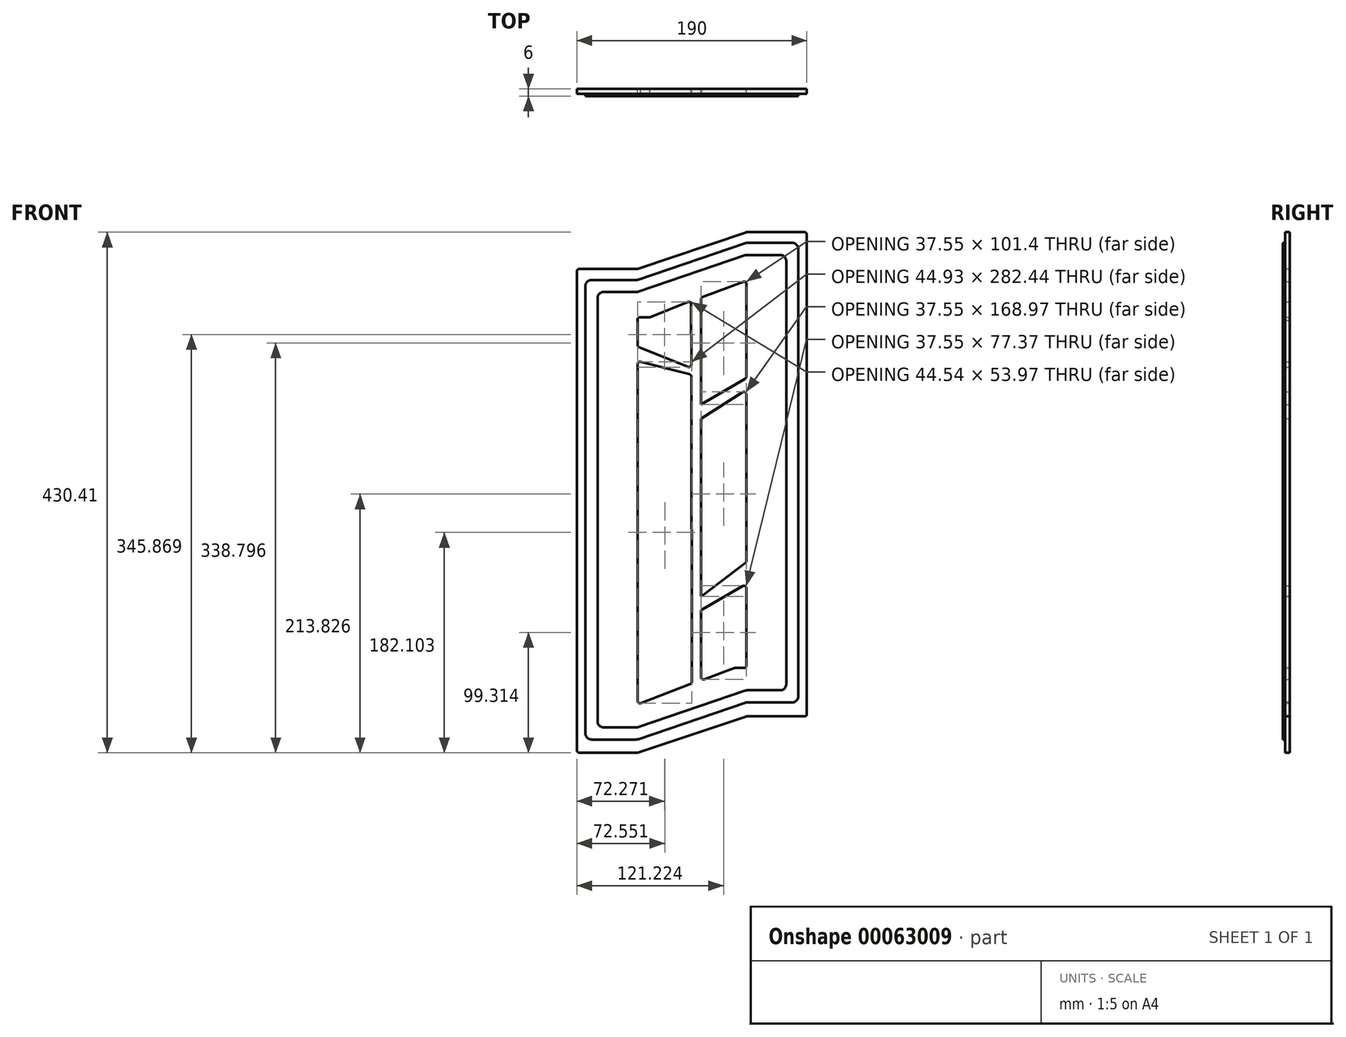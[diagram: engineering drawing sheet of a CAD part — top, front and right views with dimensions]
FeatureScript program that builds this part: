
annotation { "Feature Type Name" : "Feature", "Feature Type Description" : "" }
export const myFeature = defineFeature(function(context is Context, id is Id, definition is map)
    precondition{}
    {
        {
            var Q0;
            Q0=qCreatedBy(makeId("Front.planeOp"),FACE);
            var sketch = newSketch(context, id + "F0", { "sketchPlane" : qUnion([Q0])});
            skLineSegment(sketch, "E0", {"start": v(-0.33, 77.55) * mm, "end": v(-48, 77.55) * mm});
            skLineSegment(sketch, "E1", {"start": v(0.31, 77.65) * mm, "end": v(89.69, 107.86) * mm});
            skLineSegment(sketch, "E2", {"start": v(90.33, 107.96) * mm, "end": v(138, 107.96) * mm});
            skLineSegment(sketch, "E3", {"start": v(-48, -322.45) * mm, "end": v(-0.32, -322.45) * mm});
            skLineSegment(sketch, "E4", {"start": v(0.3, -322.35) * mm, "end": v(89.7, -292.56) * mm});
            skLineSegment(sketch, "E5", {"start": v(90.32, -292.45) * mm, "end": v(138, -292.45) * mm});
            skLineSegment(sketch, "E6", {"start": v(140, -290.45) * mm, "end": v(140, 105.96) * mm});
            skLineSegment(sketch, "E7", {"start": v(90, 107.96) * mm, "end": v(90, 67.96) * mm, "construction": true});
            skLineSegment(sketch, "E8", {"start": v(0, -322.45) * mm, "end": v(0, -282.45) * mm, "construction": true});
            skLineSegment(sketch, "E9", {"start": v(90, -292.45) * mm, "end": v(90, -252.45) * mm, "construction": true});
            skLineSegment(sketch, "E10", {"start": v(0, 77.55) * mm, "end": v(0, 37.55) * mm, "construction": true});
            skLineSegment(sketch, "E11", {"start": v(2, 37.55) * mm, "end": v(9.63, 37.55) * mm});
            skLineSegment(sketch, "E12", {"start": v(88, -252.45) * mm, "end": v(80.36, -252.45) * mm});
            skLineSegment(sketch, "E13", {"start": v(90, 65.06) * mm, "end": v(90, -250.45) * mm});
            skLineSegment(sketch, "E14", {"start": v(0, -322.45) * mm, "end": v(140, -322.45) * mm, "construction": true});
            skLineSegment(sketch, "E15", {"start": v(140, -322.45) * mm, "end": v(140, -292.45) * mm, "construction": true});
            skLineSegment(sketch, "E16", {"start": v(-50, -322.45) * mm, "end": v(-50, -361.13) * mm, "construction": true});
            skLineSegment(sketch, "E17", {"start": v(-50, -361.13) * mm, "end": v(140, -361.13) * mm, "construction": true});
            skLineSegment(sketch, "E18", {"start": v(140, -361.13) * mm, "end": v(140, -322.45) * mm, "construction": true});
            skLineSegment(sketch, "E19", {"start": v(90, 107.96) * mm, "end": v(-50, 107.96) * mm, "construction": true});
            skLineSegment(sketch, "E20", {"start": v(-50, 107.96) * mm, "end": v(-50, 77.55) * mm, "construction": true});
            skPoint(sketch, "E21.visualSharp", {"position": v(90, 67.96) * mm});
            skArc(sketch, "E21.filletArc", {"start": v(90, 65.06) * mm, "mid": v(89.14, 66.7) * mm, "end": v(87.29, 66.93) * mm});
            skPoint(sketch, "E22.visualSharp", {"position": v(10, 37.55) * mm});
            skArc(sketch, "E22.filletArc", {"start": v(9.63, 37.55) * mm, "mid": v(10, 37.58) * mm, "end": v(10.34, 37.68) * mm});
            skPoint(sketch, "E23.visualSharp", {"position": v(0, 37.55) * mm});
            skArc(sketch, "E23.filletArc", {"start": v(2, 37.55) * mm, "mid": v(0.4, 36.74) * mm, "end": v(0.09, 34.96) * mm});
            skPoint(sketch, "E24.visualSharp", {"position": v(0, -282.45) * mm});
            skArc(sketch, "E24.filletArc", {"start": v(0.09, -280.15) * mm, "mid": v(1.12, -281.36) * mm, "end": v(2.7, -281.44) * mm});
            skPoint(sketch, "E25.visualSharp", {"position": v(80, -252.45) * mm});
            skArc(sketch, "E25.filletArc", {"start": v(80.36, -252.45) * mm, "mid": v(80, -252.49) * mm, "end": v(79.66, -252.58) * mm});
            skPoint(sketch, "E26.visualSharp", {"position": v(90, -252.45) * mm});
            skArc(sketch, "E26.filletArc", {"start": v(88, -252.45) * mm, "mid": v(89.41, -251.87) * mm, "end": v(90, -250.45) * mm});
            skPoint(sketch, "E27.visualSharp", {"position": v(140, 107.96) * mm});
            skArc(sketch, "E27.filletArc", {"start": v(140, 105.96) * mm, "mid": v(139.41, 107.37) * mm, "end": v(138, 107.96) * mm});
            skPoint(sketch, "E28.visualSharp", {"position": v(90, 107.96) * mm});
            skArc(sketch, "E28.filletArc", {"start": v(90.33, 107.96) * mm, "mid": v(90, 107.93) * mm, "end": v(89.69, 107.86) * mm});
            skPoint(sketch, "E29.visualSharp", {"position": v(0, 77.55) * mm});
            skArc(sketch, "E29.filletArc", {"start": v(-0.33, 77.55) * mm, "mid": v(0, 77.57) * mm, "end": v(0.31, 77.65) * mm});
            skPoint(sketch, "E30.visualSharp", {"position": v(-50, 77.55) * mm});
            skArc(sketch, "E30.filletArc", {"start": v(-48, 77.55) * mm, "mid": v(-49.41, 76.96) * mm, "end": v(-50, 75.55) * mm});
            skPoint(sketch, "E31.visualSharp", {"position": v(-50, -322.45) * mm});
            skArc(sketch, "E31.filletArc", {"start": v(-50, -320.45) * mm, "mid": v(-49.41, -321.87) * mm, "end": v(-48, -322.45) * mm});
            skPoint(sketch, "E32.visualSharp", {"position": v(0, -322.45) * mm});
            skArc(sketch, "E32.filletArc", {"start": v(-0.32, -322.45) * mm, "mid": v(0, -322.43) * mm, "end": v(0.3, -322.35) * mm});
            skPoint(sketch, "E33.visualSharp", {"position": v(90, -292.45) * mm});
            skArc(sketch, "E33.filletArc", {"start": v(90.32, -292.45) * mm, "mid": v(90, -292.48) * mm, "end": v(89.7, -292.56) * mm});
            skPoint(sketch, "E34.visualSharp", {"position": v(140, -292.45) * mm});
            skArc(sketch, "E34.filletArc", {"start": v(138, -292.45) * mm, "mid": v(139.41, -291.87) * mm, "end": v(140, -290.45) * mm});
            skLineSegment(sketch, "E35", {"start": v(-50, -66.87) * mm, "end": v(0, -66.87) * mm, "construction": true});
            skLineSegment(sketch, "E36", {"start": v(90, -68.56) * mm, "end": v(140, -68.56) * mm, "construction": true});
            skPoint(sketch, "E37", {"position": v(52.45, 53.75) * mm});
            skLineSegment(sketch, "E38", {"start": v(52.45, 52.37) * mm, "end": v(52.45, -259.83) * mm});
            skLineSegment(sketch, "E39", {"start": v(10.34, 37.68) * mm, "end": v(41.7, 50.27) * mm});
            skPoint(sketch, "E40.visualSharp", {"position": v(44.45, 51.37) * mm});
            skArc(sketch, "E40.filletArc", {"start": v(44.45, 48.41) * mm, "mid": v(43.57, 50.07) * mm, "end": v(41.7, 50.27) * mm});
            skArc(sketch, "E41.filletArc", {"start": v(53.73, 54.24) * mm, "mid": v(52.8, 53.5) * mm, "end": v(52.45, 52.37) * mm});
            skLineSegment(sketch, "E42", {"start": v(2.7, -281.44) * mm, "end": v(43.74, -265.58) * mm});
            skPoint(sketch, "E43.visualSharp", {"position": v(45.02, -265.09) * mm});
            skArc(sketch, "E43.filletArc", {"start": v(43.74, -265.58) * mm, "mid": v(44.67, -264.85) * mm, "end": v(45.02, -263.71) * mm});
            skPoint(sketch, "E44.visualSharp", {"position": v(52.45, -262.7) * mm});
            skArc(sketch, "E44.filletArc", {"start": v(52.45, -259.83) * mm, "mid": v(53.3, -261.47) * mm, "end": v(55.14, -261.7) * mm});
            skLineSegment(sketch, "E45", {"start": v(55.14, -261.7) * mm, "end": v(79.66, -252.58) * mm});
            skLineSegment(sketch, "E46", {"start": v(-50, 75.55) * mm, "end": v(-50, -320.45) * mm});
            skLineSegment(sketch, "E47", {"start": v(0.09, -280.15) * mm, "end": v(0.09, 34.96) * mm});
            skLineSegment(sketch, "E48", {"start": v(53.73, 54.24) * mm, "end": v(87.29, 66.93) * mm});
            skLineSegment(sketch, "E49", {"start": v(44.45, 48.41) * mm, "end": v(44.45, 143.02) * mm, "construction": true});
            skLineSegment(sketch, "E50", {"start": v(44.45, 143.02) * mm, "end": v(52.45, 143.02) * mm, "construction": true});
            skLineSegment(sketch, "E51", {"start": v(52.45, 143.02) * mm, "end": v(52.45, 52.37) * mm, "construction": true});
            skLineSegment(sketch, "E52", {"start": v(1.34, 12.94) * mm, "end": v(41.79, -3.43) * mm});
            skLineSegment(sketch, "E53", {"start": v(43.05, -9.58) * mm, "end": v(2.58, 0.8) * mm});
            skLineSegment(sketch, "E54", {"start": v(52.45, -34.35) * mm, "end": v(89, -13.1) * mm});
            skLineSegment(sketch, "E55", {"start": v(52.45, -46.2) * mm, "end": v(52.45, -34.35) * mm});
            skLineSegment(sketch, "E56", {"start": v(0.09, -64.55) * mm, "end": v(0.09, -109.83) * mm});
            skLineSegment(sketch, "E57", {"start": v(0.9, -111.44) * mm, "end": v(43.99, -143.2) * mm});
            skLineSegment(sketch, "E58", {"start": v(41.3, -130.68) * mm, "end": v(19.19, -106.6) * mm});
            skLineSegment(sketch, "E59", {"start": v(18.66, -66.36) * mm, "end": v(18.66, -105.25) * mm});
            skPoint(sketch, "E60", {"position": v(44.63, -50.8) * mm});
            skLineSegment(sketch, "E61", {"start": v(0.09, -213.67) * mm, "end": v(0.09, -213.67) * mm});
            skLineSegment(sketch, "E62", {"start": v(44.45, 48.41) * mm, "end": v(45.02, -263.71) * mm});
            skLineSegment(sketch, "E63", {"start": v(44.92, -203.7) * mm, "end": v(44.94, -209.15) * mm});
            skLineSegment(sketch, "E64", {"start": v(44.96, -231.01) * mm, "end": v(44.96, -231.51) * mm});
            skLineSegment(sketch, "E65", {"start": v(44.9, -198.69) * mm, "end": v(44.9, -195.84) * mm});
            skLineSegment(sketch, "E66", {"start": v(52.45, -192.66) * mm, "end": v(52.45, -191.64) * mm});
            skPoint(sketch, "E67.visualSharp", {"position": v(52.45, -193.61) * mm});
            skArc(sketch, "E67.filletArc", {"start": v(52.45, -192.66) * mm, "mid": v(52.7, -193.07) * mm, "end": v(53.19, -193) * mm});
            skLineSegment(sketch, "E68", {"start": v(52.45, -205.71) * mm, "end": v(52.45, -208.68) * mm});
            skPoint(sketch, "E69.visualSharp", {"position": v(52.45, -205.45) * mm});
            skArc(sketch, "E69.filletArc", {"start": v(53.45, -203.98) * mm, "mid": v(52.72, -204.7) * mm, "end": v(52.45, -205.71) * mm});
            skLineSegment(sketch, "E70", {"start": v(44.92, -211.09) * mm, "end": v(44.92, -212.4) * mm});
            skLineSegment(sketch, "E71", {"start": v(44.95, -228.59) * mm, "end": v(44.95, -229.06) * mm});
            skPoint(sketch, "E72.visualSharp", {"position": v(44.95, -229.84) * mm});
            skLineSegment(sketch, "E73", {"start": v(53.19, -193) * mm, "end": v(89.21, -165.52) * mm});
            skLineSegment(sketch, "E74", {"start": v(90, -163.93) * mm, "end": v(90, -158.71) * mm});
            skLineSegment(sketch, "E75", {"start": v(53.45, -203.98) * mm, "end": v(87, -184.72) * mm});
            skLineSegment(sketch, "E76", {"start": v(90, -186.45) * mm, "end": v(90, -189.1) * mm});
            skPoint(sketch, "E77.visualSharp", {"position": v(90, -183) * mm});
            skArc(sketch, "E77.filletArc", {"start": v(90, -186.45) * mm, "mid": v(89, -184.72) * mm, "end": v(87, -184.72) * mm});
            skPoint(sketch, "E78.visualSharp", {"position": v(90, -164.92) * mm});
            skArc(sketch, "E78.filletArc", {"start": v(89.21, -165.52) * mm, "mid": v(89.8, -164.82) * mm, "end": v(90, -163.93) * mm});
            skLineSegment(sketch, "E79", {"start": v(44.92, -212.4) * mm, "end": v(44.95, -228.59) * mm});
            skLineSegment(sketch, "E80", {"start": v(44.77, -129.32) * mm, "end": v(44.63, -54.2) * mm});
            skPoint(sketch, "E81.visualSharp", {"position": v(44.78, -134.47) * mm});
            skArc(sketch, "E81.filletArc", {"start": v(41.3, -130.68) * mm, "mid": v(43.5, -131.19) * mm, "end": v(44.77, -129.32) * mm});
            skLineSegment(sketch, "E82", {"start": v(44.8, -144.81) * mm, "end": v(44.8, -148.78) * mm});
            skPoint(sketch, "E83.visualSharp", {"position": v(44.8, -143.8) * mm});
            skArc(sketch, "E83.filletArc", {"start": v(44.8, -144.81) * mm, "mid": v(44.58, -143.91) * mm, "end": v(43.99, -143.2) * mm});
            skPoint(sketch, "E84.visualSharp", {"position": v(18.66, -106.03) * mm});
            skArc(sketch, "E84.filletArc", {"start": v(18.66, -105.25) * mm, "mid": v(18.8, -105.98) * mm, "end": v(19.19, -106.6) * mm});
            skPoint(sketch, "E85.visualSharp", {"position": v(0.09, -110.84) * mm});
            skArc(sketch, "E85.filletArc", {"start": v(0.09, -109.83) * mm, "mid": v(0.3, -110.73) * mm, "end": v(0.9, -111.44) * mm});
            skPoint(sketch, "E86.visualSharp", {"position": v(18.66, -65.18) * mm});
            skArc(sketch, "E86.filletArc", {"start": v(19.7, -64.61) * mm, "mid": v(18.94, -65.35) * mm, "end": v(18.66, -66.36) * mm});
            skPoint(sketch, "E87.visualSharp", {"position": v(0.09, -63.37) * mm});
            skArc(sketch, "E87.filletArc", {"start": v(1.12, -62.8) * mm, "mid": v(0.36, -63.53) * mm, "end": v(0.09, -64.55) * mm});
            skLineSegment(sketch, "E88", {"start": v(44.6, -37.54) * mm, "end": v(44.6, -37.52) * mm});
            skLineSegment(sketch, "E89", {"start": v(52.45, -46.2) * mm, "end": v(86.93, -24.45) * mm});
            skLineSegment(sketch, "E90", {"start": v(90, -11.36) * mm, "end": v(90, -10.05) * mm});
            skPoint(sketch, "E91.visualSharp", {"position": v(90, -12.51) * mm});
            skArc(sketch, "E91.filletArc", {"start": v(89, -13.1) * mm, "mid": v(89.73, -12.36) * mm, "end": v(90, -11.36) * mm});
            skLineSegment(sketch, "E92", {"start": v(0.09, 14.8) * mm, "end": v(0.09, 18.42) * mm});
            skPoint(sketch, "E93.visualSharp", {"position": v(0.09, 13.45) * mm});
            skArc(sketch, "E93.filletArc", {"start": v(0.09, 14.8) * mm, "mid": v(0.43, 13.68) * mm, "end": v(1.34, 12.94) * mm});
            skLineSegment(sketch, "E94", {"start": v(0.09, -1.13) * mm, "end": v(0.09, -3.75) * mm});
            skLineSegment(sketch, "E95", {"start": v(44.54, -1.57) * mm, "end": v(44.53, 2.19) * mm});
            skLineSegment(sketch, "E96", {"start": v(44.56, -11.51) * mm, "end": v(44.57, -17.55) * mm});
            skPoint(sketch, "E97.visualSharp", {"position": v(0.09, 1.45) * mm});
            skArc(sketch, "E97.filletArc", {"start": v(2.58, 0.8) * mm, "mid": v(0.86, 0.45) * mm, "end": v(0.09, -1.13) * mm});
            skPoint(sketch, "E98.visualSharp", {"position": v(44.54, -4.55) * mm});
            skArc(sketch, "E98.filletArc", {"start": v(41.79, -3.43) * mm, "mid": v(43.66, -3.23) * mm, "end": v(44.54, -1.57) * mm});
            skPoint(sketch, "E99.visualSharp", {"position": v(44.55, -9.96) * mm});
            skArc(sketch, "E99.filletArc", {"start": v(44.56, -11.51) * mm, "mid": v(44.14, -10.29) * mm, "end": v(43.05, -9.58) * mm});
            skLineSegment(sketch, "E100", {"start": v(90, -26.14) * mm, "end": v(90, -29.1) * mm});
            skPoint(sketch, "E101.visualSharp", {"position": v(90, -22.51) * mm});
            skArc(sketch, "E101.filletArc", {"start": v(90, -26.14) * mm, "mid": v(88.97, -24.39) * mm, "end": v(86.93, -24.45) * mm});
            skLineSegment(sketch, "E102", {"start": v(1.12, -62.8) * mm, "end": v(44.6, -38.72) * mm});
            skLineSegment(sketch, "E103", {"start": v(19.7, -64.61) * mm, "end": v(44.63, -50.8) * mm});
            skSolve(sketch);
        }
        {
            var Q0;
            Q0=makeQuery(id+"F0.imprint","IMPRINT",FACE,{"disambiguationData":[TD([[makeQuery(id+"F0.imprint","IMPRINT",EDGE,{"derivedFrom":sQuery(id+"F0.wireOp",EDGE,"E0")}),1.0]])]});
            var Q1;
            Q1=makeQuery(id+"F0.imprint","IMPRINT",FACE,{"disambiguationData":[TD([[makeQuery(id+"F0.imprint","IMPRINT",EDGE,{"derivedFrom":sQuery(id+"F0.wireOp",EDGE,"E54")}),-1.0]])]});
            var Q2;
            Q2=makeQuery(id+"F0.imprint","IMPRINT",FACE,{"disambiguationData":[TD([[makeQuery(id+"F0.imprint","IMPRINT",EDGE,{"derivedFrom":sQuery(id+"F0.wireOp",EDGE,"E52")}),-1.0]])]});
            var Q3;
            Q3=makeQuery(id+"F0.imprint","IMPRINT",FACE,{"disambiguationData":[TD([[makeQuery(id+"F0.imprint","IMPRINT",EDGE,{"derivedFrom":sQuery(id+"F0.wireOp",EDGE,"E56")}),1.0]])]});
            var Q4;
            {var subQ1=sQuery(id+"F0.wireOp",EDGE,"E67.filletArc");Q4=makeQuery(id+"F0.imprint","IMPRINT",FACE,{"disambiguationData":[TD([[makeQuery(id+"F0.imprint","IMPRINT",EDGE,{"derivedFrom":subQ1}),-1.0]])]});}
            extrude(context, id + "F1", {"entities" : qUnion([Q0, Q1, Q2, Q3, Q4]), "depth" : 4 * mm});
        }
        {
            var Q0;
            Q0=makeQuery(id+"F0.imprint","IMPRINT",FACE,{"disambiguationData":[TD([[makeQuery(id+"F0.imprint","IMPRINT",EDGE,{"derivedFrom":sQuery(id+"F0.wireOp",EDGE,"E0")}),1.0]])]});
            var sketch = newSketch(context, id + "F2", { "sketchPlane" : qUnion([Q0])});
            skLineSegment(sketch, "E104", {"start": v(132.91, 94.13) * mm, "end": v(132.91, -275.87) * mm});
            skLineSegment(sketch, "E105", {"start": v(127.91, -280.87) * mm, "end": v(90.74, -280.87) * mm});
            skLineSegment(sketch, "E106", {"start": v(89.13, -281.14) * mm, "end": v(0.78, -311.27) * mm});
            skLineSegment(sketch, "E107", {"start": v(-0.83, -311.53) * mm, "end": v(-38, -311.53) * mm});
            skLineSegment(sketch, "E108", {"start": v(-43, -306.53) * mm, "end": v(-43, 63.47) * mm});
            skLineSegment(sketch, "E109", {"start": v(-38, 68.47) * mm, "end": v(-0.83, 68.47) * mm});
            skLineSegment(sketch, "E110", {"start": v(0.78, 68.73) * mm, "end": v(89.13, 98.86) * mm});
            skLineSegment(sketch, "E111", {"start": v(90.74, 99.13) * mm, "end": v(127.91, 99.13) * mm});
            skLineSegment(sketch, "E112", {"start": v(122.91, -270.87) * mm, "end": v(132.91, -270.87) * mm, "construction": true});
            skLineSegment(sketch, "E113", {"start": v(122.91, -280.87) * mm, "end": v(122.91, -270.87) * mm, "construction": true});
            skLineSegment(sketch, "E114", {"start": v(89.91, -280.87) * mm, "end": v(89.91, -270.87) * mm, "construction": true});
            skLineSegment(sketch, "E115", {"start": v(0, -311.53) * mm, "end": v(0, -301.53) * mm, "construction": true});
            skLineSegment(sketch, "E116", {"start": v(-43, -301.53) * mm, "end": v(-33, -301.53) * mm, "construction": true});
            skLineSegment(sketch, "E117", {"start": v(-33, -301.53) * mm, "end": v(-33, -311.53) * mm, "construction": true});
            skLineSegment(sketch, "E118", {"start": v(-33, 68.47) * mm, "end": v(-33, 58.47) * mm, "construction": true});
            skLineSegment(sketch, "E119", {"start": v(-33, 58.47) * mm, "end": v(-43, 58.47) * mm, "construction": true});
            skLineSegment(sketch, "E120", {"start": v(0, 68.47) * mm, "end": v(0, 58.47) * mm, "construction": true});
            skLineSegment(sketch, "E121", {"start": v(89.91, 99.13) * mm, "end": v(89.91, 89.13) * mm, "construction": true});
            skLineSegment(sketch, "E122", {"start": v(122.91, 99.13) * mm, "end": v(122.91, 89.13) * mm, "construction": true});
            skLineSegment(sketch, "E123", {"start": v(122.91, 89.13) * mm, "end": v(132.91, 89.13) * mm, "construction": true});
            skLineSegment(sketch, "E124", {"start": v(117.91, -270.87) * mm, "end": v(90.74, -270.87) * mm});
            skLineSegment(sketch, "E125", {"start": v(89.13, -271.14) * mm, "end": v(0.78, -301.27) * mm});
            skLineSegment(sketch, "E126", {"start": v(-0.83, -301.53) * mm, "end": v(-28, -301.53) * mm});
            skLineSegment(sketch, "E127", {"start": v(-33, -296.53) * mm, "end": v(-33, 53.47) * mm});
            skLineSegment(sketch, "E128", {"start": v(-28, 58.47) * mm, "end": v(-0.83, 58.47) * mm});
            skLineSegment(sketch, "E129", {"start": v(0.78, 58.73) * mm, "end": v(89.13, 88.86) * mm});
            skLineSegment(sketch, "E130", {"start": v(90.74, 89.13) * mm, "end": v(117.91, 89.13) * mm});
            skLineSegment(sketch, "E131", {"start": v(122.91, 84.13) * mm, "end": v(122.91, -265.87) * mm});
            skPoint(sketch, "E132.visualSharp", {"position": v(89.91, -270.87) * mm});
            skArc(sketch, "E132.filletArc", {"start": v(90.74, -270.87) * mm, "mid": v(89.93, -270.94) * mm, "end": v(89.13, -271.14) * mm});
            skPoint(sketch, "E133.visualSharp", {"position": v(122.91, -270.87) * mm});
            skArc(sketch, "E133.filletArc", {"start": v(117.91, -270.87) * mm, "mid": v(121.45, -269.4) * mm, "end": v(122.91, -265.87) * mm});
            skPoint(sketch, "E134.visualSharp", {"position": v(132.91, -280.87) * mm});
            skArc(sketch, "E134.filletArc", {"start": v(127.91, -280.87) * mm, "mid": v(131.45, -279.4) * mm, "end": v(132.91, -275.87) * mm});
            skPoint(sketch, "E135.visualSharp", {"position": v(89.91, -280.87) * mm});
            skArc(sketch, "E135.filletArc", {"start": v(90.74, -280.87) * mm, "mid": v(89.93, -280.94) * mm, "end": v(89.13, -281.14) * mm});
            skPoint(sketch, "E136.visualSharp", {"position": v(0, -301.53) * mm});
            skArc(sketch, "E136.filletArc", {"start": v(-0.83, -301.53) * mm, "mid": v(-0.01, -301.47) * mm, "end": v(0.78, -301.27) * mm});
            skPoint(sketch, "E137.visualSharp", {"position": v(0, -311.53) * mm});
            skArc(sketch, "E137.filletArc", {"start": v(-0.83, -311.53) * mm, "mid": v(-0.01, -311.47) * mm, "end": v(0.78, -311.27) * mm});
            skPoint(sketch, "E138.visualSharp", {"position": v(-33, -301.53) * mm});
            skArc(sketch, "E138.filletArc", {"start": v(-33, -296.53) * mm, "mid": v(-31.54, -300.07) * mm, "end": v(-28, -301.53) * mm});
            skPoint(sketch, "E139.visualSharp", {"position": v(-43, -311.53) * mm});
            skArc(sketch, "E139.filletArc", {"start": v(-43, -306.53) * mm, "mid": v(-41.54, -310.07) * mm, "end": v(-38, -311.53) * mm});
            skPoint(sketch, "E140.visualSharp", {"position": v(-33, 58.47) * mm});
            skArc(sketch, "E140.filletArc", {"start": v(-28, 58.47) * mm, "mid": v(-31.54, 57) * mm, "end": v(-33, 53.47) * mm});
            skPoint(sketch, "E141.visualSharp", {"position": v(-43, 68.47) * mm});
            skArc(sketch, "E141.filletArc", {"start": v(-38, 68.47) * mm, "mid": v(-41.54, 67) * mm, "end": v(-43, 63.47) * mm});
            skPoint(sketch, "E142.visualSharp", {"position": v(0, 68.47) * mm});
            skArc(sketch, "E142.filletArc", {"start": v(-0.83, 68.47) * mm, "mid": v(-0.01, 68.53) * mm, "end": v(0.78, 68.73) * mm});
            skPoint(sketch, "E143.visualSharp", {"position": v(0, 58.47) * mm});
            skArc(sketch, "E143.filletArc", {"start": v(-0.83, 58.47) * mm, "mid": v(-0.01, 58.53) * mm, "end": v(0.78, 58.73) * mm});
            skPoint(sketch, "E144.visualSharp", {"position": v(89.91, 99.13) * mm});
            skArc(sketch, "E144.filletArc", {"start": v(90.74, 99.13) * mm, "mid": v(89.93, 99.06) * mm, "end": v(89.13, 98.86) * mm});
            skPoint(sketch, "E145.visualSharp", {"position": v(89.91, 89.13) * mm});
            skArc(sketch, "E145.filletArc", {"start": v(90.74, 89.13) * mm, "mid": v(89.93, 89.06) * mm, "end": v(89.13, 88.86) * mm});
            skPoint(sketch, "E146.visualSharp", {"position": v(122.91, 89.13) * mm});
            skArc(sketch, "E146.filletArc", {"start": v(122.91, 84.13) * mm, "mid": v(121.45, 87.67) * mm, "end": v(117.91, 89.13) * mm});
            skPoint(sketch, "E147.visualSharp", {"position": v(132.91, 99.13) * mm});
            skArc(sketch, "E147.filletArc", {"start": v(132.91, 94.13) * mm, "mid": v(131.45, 97.67) * mm, "end": v(127.91, 99.13) * mm});
            skSolve(sketch);
        }
        {
            var Q0;
            Q0 = qSketchRegion(id + "F2", true);
            extrude(context, id + "F3", {"entities" : qUnion([Q0]), "operationType" : NewBodyOperationType.ADD, "depth" : 6 * mm});
        }
    });
